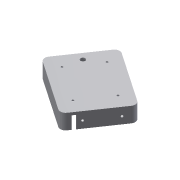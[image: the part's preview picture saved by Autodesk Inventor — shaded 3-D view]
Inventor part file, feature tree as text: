
AUTODESK INVENTOR PART (.ipt)
format: ipt  version: 2014 SP2 (Build 180246200, 246)  size: 276,992 bytes
history: native  units: mm
features: sketch x10, other x9, projected_geometry x8, extrude x7, hole x3, pattern_linear x2, chamfer x2
ambient origin geometry x8: Origin, YZ Plane, XZ Plane, XY Plane, X Axis, Y Axis, Z Axis, Center Point
bodies: Body1 (feature_tree)
feature tree (41):
  other  "Těleso1"
  extrude  "Vysunutí1"  Depth=2.0mm TaperAngle=0.0deg
  extrude  "Vysunutí2"  Depth=2.0mm
  extrude  "Vysunutí3"  Depth=21.0mm TaperAngle=0.0deg
  extrude  "Vysunutí4"  Depth=5.0mm
  hole  "Díra1"  [1 undecoded]
  extrude  "Vysunutí5"  Depth=4.0mm
  hole  "Díra2"  [1 undecoded]
  pattern_linear  "Obdélníkové pole1"  Spacing1=2.36mm  [1 undecoded]
  extrude  "Vysunutí6"  Depth=10.279mm
  extrude  "Vysunutí7"  Depth=4.0mm
  pattern_linear  "Obdélníkové pole2"  Spacing1=17.75mm  [1 undecoded]
  chamfer  "Zkosení1"  Distance=42.0mm
  chamfer  "Zkosení2"  Distance=42.0mm
  hole  "Díra3"  [1 undecoded]
  sketch  "Náčrt4"
  other  "Referenční1"
  other  "Referenční2"
  other  "Referenční3"
  other  "Referenční4"
  other  "Referenční5"
  other  "Referenční6"
  other  "Referenční7"
  other  "Referenční8"
  sketch  "Náčrt5"
  projected_geometry  "Promítnutá smyčka1"
  sketch  "Náčrt7"
  projected_geometry  "Promítnutá smyčka2"
  sketch  "Náčrt8"
  projected_geometry  "Promítnutá smyčka3"
  sketch  "Náčrt9"
  projected_geometry  "Promítnutá smyčka4"
  sketch  "Náčrt10"
  projected_geometry  "Promítnutá smyčka5"
  sketch  "Náčrt11"
  sketch  "Náčrt12"
  projected_geometry  "Promítnutá smyčka6"
  sketch  "Náčrt13"
  projected_geometry  "Promítnutá smyčka7"
  sketch  "Náčrt14"
  projected_geometry  "Promítnutá smyčka8"
note: 5 required parameter values undecoded (feature->parameter linkage not recoverable at this tier; creation-order binding heuristic only, values carry confidence <= 0.55)
